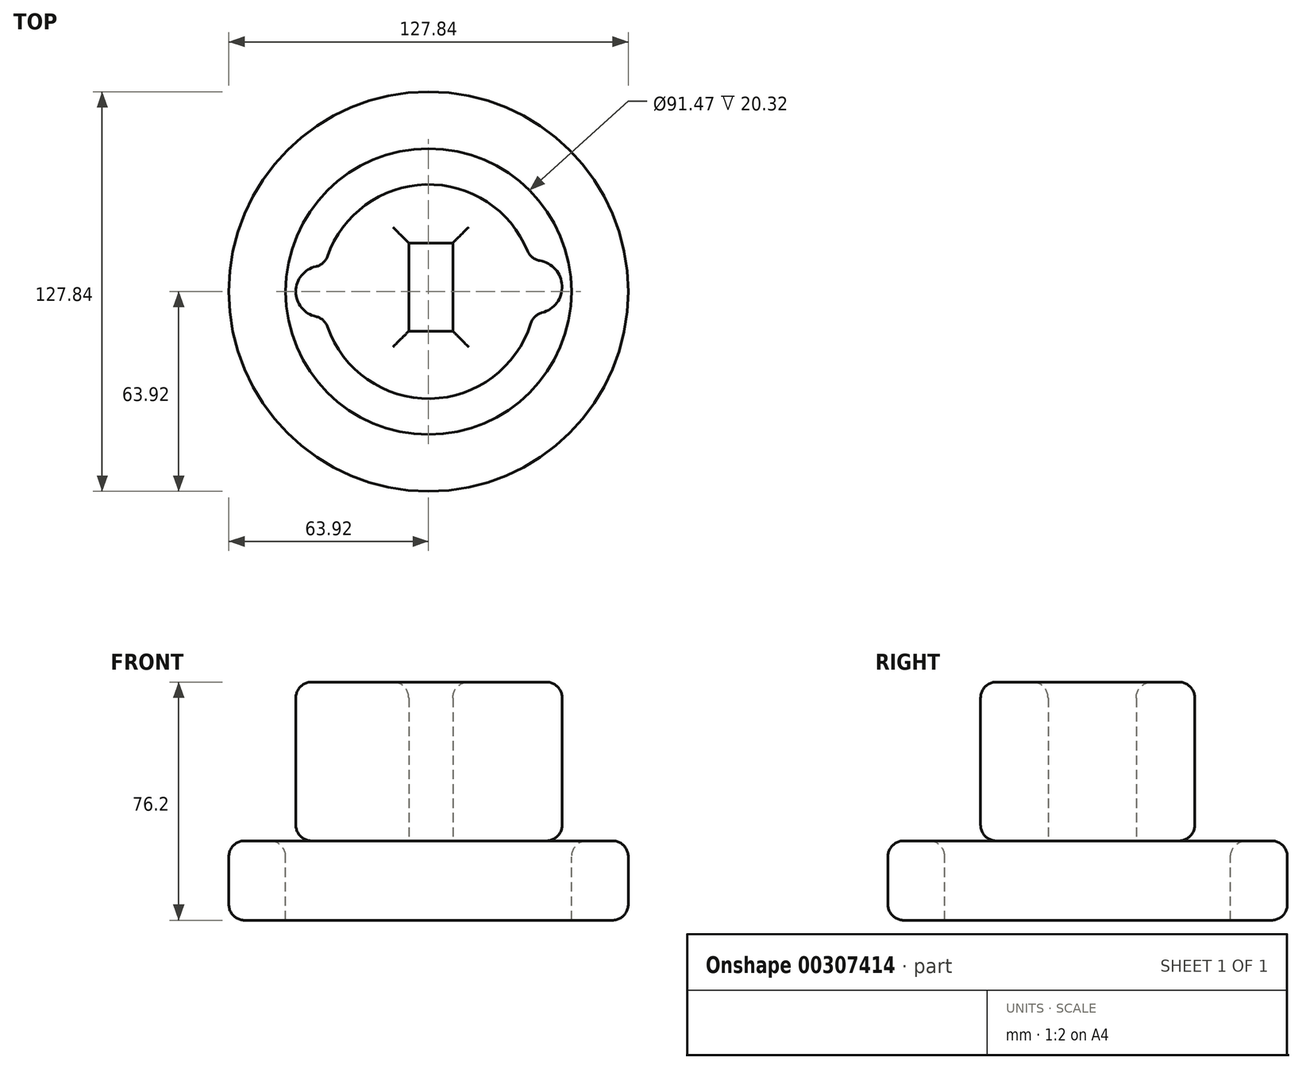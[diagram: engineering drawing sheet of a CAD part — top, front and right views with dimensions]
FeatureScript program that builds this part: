
annotation { "Feature Type Name" : "Feature", "Feature Type Description" : "" }
export const myFeature = defineFeature(function(context is Context, id is Id, definition is map)
    precondition{}
    {
        {
            var Q0;
            Q0=qCreatedBy(makeId("Top.planeOp"),FACE);
            var sketch = newSketch(context, id + "F0", { "sketchPlane" : qUnion([Q0])});
            skCircle(sketch, "E0", {"center": v(0, 0) * mm, "radius": 63.92 * mm});
            skCircle(sketch, "E1", {"center": v(0, 0) * mm, "radius": 45.73 * mm});
            skArc(sketch, "E2", {"start": v(-33.28, -8.14) * mm, "mid": v(0.58, -34.25) * mm, "end": v(33.54, -7) * mm});
            skLineSegment(sketch, "E3", {"start": v(-63.92, 0) * mm, "end": v(63.92, 0) * mm, "construction": true});
            skArc(sketch, "E4", {"start": v(32.23, 0) * mm, "mid": v(33.28, 0.68) * mm, "end": v(34.23, 1.49) * mm, "construction": true});
            skArc(sketch, "E5", {"start": v(33.54, -7) * mm, "mid": v(39.96, 7.79) * mm, "end": v(25.84, 0) * mm});
            skArc(sketch, "E6", {"start": v(-33.28, 8.14) * mm, "mid": v(-42.45, 0) * mm, "end": v(-33.28, -8.14) * mm});
            skArc(sketch, "E7.trimOffspring", {"start": v(32.8, 9.89) * mm, "mid": v(-0.9, 34.25) * mm, "end": v(-33.28, 8.14) * mm});
            skArc(sketch, "E8.trimOffspring", {"start": v(34.26, 0) * mm, "mid": v(34.25, 0.74) * mm, "end": v(34.23, 1.49) * mm});
            skLineSegment(sketch, "E9", {"start": v(0, 63.92) * mm, "end": v(0, 45.73) * mm, "construction": true});
            skLineSegment(sketch, "E10.bottom", {"start": v(-6.33, 15.54) * mm, "end": v(7.77, 15.54) * mm});
            skLineSegment(sketch, "E10.top", {"start": v(-6.33, -12.66) * mm, "end": v(7.77, -12.66) * mm});
            skLineSegment(sketch, "E10.left", {"start": v(-6.33, 15.54) * mm, "end": v(-6.33, -12.66) * mm});
            skLineSegment(sketch, "E10.right", {"start": v(7.77, 15.54) * mm, "end": v(7.77, -12.66) * mm});
            skSolve(sketch);
        }
        {
            var Q0;
            Q0 = qSketchRegion(id + "F0", true);
            extrude(context, id + "F1", {"entities" : qUnion([Q0]), "oppositeDirection" : true, "depth" : 25.4 * mm});
        }
        {
            var Q0;
            {var subQ2=sQuery(id+"F0.wireOp",EDGE,"E2");Q0=makeQuery(id+"F0.imprint","IMPRINT",FACE,{"disambiguationData":[TD([[makeQuery(id+"F0.imprint","IMPRINT",EDGE,{"derivedFrom":subQ2}),1.0]])]});}
            extrude(context, id + "F2", {"entities" : qUnion([Q0]), "depth" : 25.4 * mm});
        }
        {
            var Q0;
            Q0=makeQuery(id+"F2.opExtrude","CAP_FACE",FACE,{"disambiguationData":[OSD([sQuery(id+"F0.wireOp",EDGE,"E2"),sQuery(id+"F0.wireOp",EDGE,"E5"),sQuery(id+"F0.wireOp",EDGE,"E6"),sQuery(id+"F0.wireOp",EDGE,"E7.trimOffspring"),sQuery(id+"F0.wireOp",EDGE,"E10.bottom"),sQuery(id+"F0.wireOp",EDGE,"E10.top"),sQuery(id+"F0.wireOp",EDGE,"E10.left"),sQuery(id+"F0.wireOp",EDGE,"E10.right")])],"isStart":false});
            extrude(context, id + "F3", {"entities" : qUnion([Q0]), "operationType" : NewBodyOperationType.ADD, "depth" : 25.4 * mm});
        }
        {
            var Q0;
            {var subQ0=sQuery(id+"F0.wireOp",EDGE,"E2");Q0=makeQuery(id+"F3.boolean.opBoolean","MERGE",FACE,{"derivedFrom":[makeQuery(id+"F2.opExtrude","SWEPT_FACE",FACE,{"disambiguationData":[OSD([subQ0])]}),makeQuery(id+"F3.opExtrude","SWEPT_FACE",FACE,{"disambiguationData":[OSD([subQ0])]})]});}
            var Q1;
            {var subQ0=sQuery(id+"F0.wireOp",EDGE,"E5");Q1=makeQuery(id+"F3.boolean.opBoolean","MERGE",FACE,{"derivedFrom":[makeQuery(id+"F2.opExtrude","SWEPT_FACE",FACE,{"disambiguationData":[OSD([subQ0])]}),makeQuery(id+"F3.opExtrude","SWEPT_FACE",FACE,{"disambiguationData":[OSD([subQ0])]})]});}
            var Q2;
            Q2=makeQuery(id+"F3.opExtrude","CAP_EDGE",EDGE,{"disambiguationData":[OSD([sQuery(id+"F0.wireOp",EDGE,"E7.trimOffspring")])],"isStart":false});
            var Q3;
            Q3=makeQuery(id+"F3.opExtrude","CAP_FACE",FACE,{"disambiguationData":[OSD([sQuery(id+"F0.wireOp",EDGE,"E2"),sQuery(id+"F0.wireOp",EDGE,"E5"),sQuery(id+"F0.wireOp",EDGE,"E6"),sQuery(id+"F0.wireOp",EDGE,"E7.trimOffspring"),sQuery(id+"F0.wireOp",EDGE,"E10.bottom"),sQuery(id+"F0.wireOp",EDGE,"E10.top"),sQuery(id+"F0.wireOp",EDGE,"E10.left"),sQuery(id+"F0.wireOp",EDGE,"E10.right")])],"isStart":false});
            var Q4;
            Q4=makeQuery(id+"F3.opExtrude","CAP_EDGE",EDGE,{"disambiguationData":[OSD([sQuery(id+"F0.wireOp",EDGE,"E2")])],"isStart":false});
            var Q5;
            {var subQ0=sQuery(id+"F0.wireOp",EDGE,"E6");Q5=makeQuery(id+"F3.boolean.opBoolean","MERGE",FACE,{"derivedFrom":[makeQuery(id+"F2.opExtrude","SWEPT_FACE",FACE,{"disambiguationData":[OSD([subQ0])]}),makeQuery(id+"F3.opExtrude","SWEPT_FACE",FACE,{"disambiguationData":[OSD([subQ0])]})]});}
            fillet(context, id + "F4", {"entities" : qUnion([Q0, Q1, Q2, Q3, Q4, Q5]), "radius" : 5.08 * mm, "tangentPropagation" : true, "allowEdgeOverflow" : false});
        }
        {
            var Q0;
            Q0=makeQuery(id+"F1.opExtrude","SWEPT_FACE",FACE,{"disambiguationData":[OSD([sQuery(id+"F0.wireOp",EDGE,"E0")])]});
            var Q1;
            Q1=makeQuery(id+"F1.opExtrude","CAP_EDGE",EDGE,{"disambiguationData":[OSD([sQuery(id+"F0.wireOp",EDGE,"E1")])],"isStart":true});
            fillet(context, id + "F5", {"entities" : qUnion([Q0, Q1]), "radius" : 5.08 * mm, "tangentPropagation" : true, "allowEdgeOverflow" : false});
        }
        {
            var Q0;
            {var subQ0=sQuery(id+"F0.wireOp",EDGE,"E7.trimOffspring");Q0=makeQuery(id+"F3.boolean.opBoolean","MERGE",FACE,{"derivedFrom":[makeQuery(id+"F2.opExtrude","SWEPT_FACE",FACE,{"disambiguationData":[OSD([subQ0])]}),makeQuery(id+"F3.opExtrude","SWEPT_FACE",FACE,{"disambiguationData":[OSD([subQ0])]})]});}
            var Q1;
            Q1=makeQuery(id+"F3.opExtrude","CAP_FACE",FACE,{"disambiguationData":[OSD([sQuery(id+"F0.wireOp",EDGE,"E2"),sQuery(id+"F0.wireOp",EDGE,"E5"),sQuery(id+"F0.wireOp",EDGE,"E6"),sQuery(id+"F0.wireOp",EDGE,"E7.trimOffspring"),sQuery(id+"F0.wireOp",EDGE,"E10.bottom"),sQuery(id+"F0.wireOp",EDGE,"E10.top"),sQuery(id+"F0.wireOp",EDGE,"E10.left"),sQuery(id+"F0.wireOp",EDGE,"E10.right")])],"isStart":false});
            var Q2;
            {var subQ0=sQuery(id+"F0.wireOp",EDGE,"E5");Q2=makeQuery(id+"F3.boolean.opBoolean","MERGE",FACE,{"derivedFrom":[makeQuery(id+"F2.opExtrude","SWEPT_FACE",FACE,{"disambiguationData":[OSD([subQ0])]}),makeQuery(id+"F3.opExtrude","SWEPT_FACE",FACE,{"disambiguationData":[OSD([subQ0])]})]});}
            fillet(context, id + "F6", {"entities" : qUnion([Q0, Q1, Q2]), "radius" : 5.08 * mm, "tangentPropagation" : true, "allowEdgeOverflow" : false});
        }
    });
